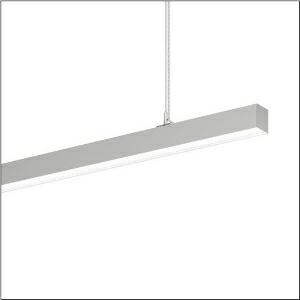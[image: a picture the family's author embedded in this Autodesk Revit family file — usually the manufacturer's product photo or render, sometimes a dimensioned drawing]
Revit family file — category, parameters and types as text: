
# Revit family: silica_r__21_51mx30db45sb_ca73
name_source: partatom
category: Lighting Fixtures
units: mm (PartAtom-declared; Revit-internal decimal feet)

## family parameters
Cut with Voids When Loaded = No
Host = Face
Light Source = No
Part Type = Normal
Room Calculation Point = No
Round Connector Dimension = Use Diameter
Shared = No

## types (1)
- --- (1 x LED, 5260 lm, 32 W, 4000K)
    Apparent Load = 32 VA
    CIE Flux Codes = 47 79 96 57 100
    Color Rendering = 80
    Color Temperature = 4000K
    Default Elevation = 1800 mm
    Description = Silica® 21, office luminaire, primary optical cover: cover, of PMMA, opal, light emission: direct/indirect distribution, primary light characteristic: symmetric, installation type: suspended mounting, LED, rated luminous flux: 5.260lm, luminous efficacy: 164lm/W, light colour: 840, colour temperature: 4000K, with terminal, 3+2-pole, max. 2.5mm², mains connection: 220..240V, AC, 50/60Hz, rated input power: 32W, luminaire housing, of aluminium, metallic grey (RAL 9006), length: 1.504mm, width: 53mm, height: 53mm, protection rating (complete): IP20, insulation class (complete): insulation class I (protective earthing), certification: CE, permissible operating ambient temperature: 0..+35°C, standard: EN 50419, packaging unit: 1 piece
    Height = 53 mm
    Lamp = 1 x LED
    Lamp Light Flux = 5260 lm
    Lamp Power = 32 W
    Lamp count = 1
    Length = 1504 mm
    Luminous efficacy = 164 lm/W
    Manufacturer = Siteco
    ModVariant = No
    Model = 51MX30DB45SB
    Mounting Place = Ceiling
    Mounting Type = Pendant
    Number of Poles = 1
    OnlyDefault = Yes
    Power Factor = 1
    Product Name = Silica® 21
    Product group = office luminaire | ceiling pendant
    ProductGroupID = 905
    Protection Class = Protection class I
    Protection Degree = IP 20
    RLX_Detail_Level = 1
    RlxData = <blob elided: 23325 chars, md5=453b2752>
    Socket = socket
    Standby Power = 0 W
    System Light Flux = 5260 lm
    System Power = 32 W
    Type Comments = factory setting: luminous flux: 100 % | dim-lin: 254 | 218 mA
    Type Image = l_1251727.jpg
    URL = http://relux.com
    VarID = @adj_025339
    Voltage = 0 V
    Weight = 0.00 kg
    Width = 53 mm

## geometry (parser evidence)
native form markers: Blend x4, Sweep x13
no freeform markers — native parametric forms only
